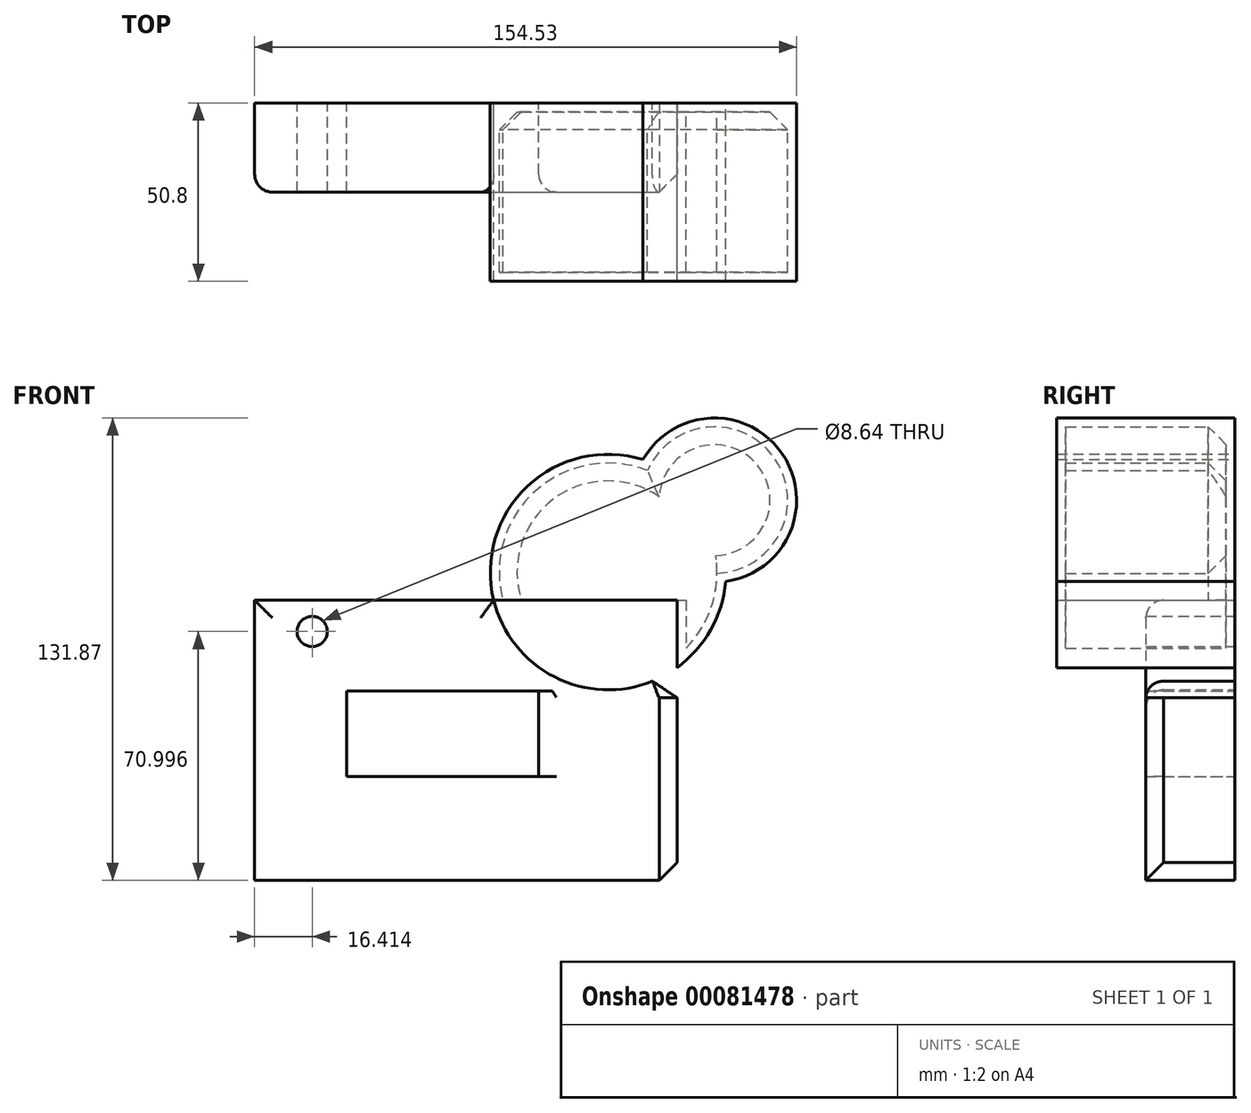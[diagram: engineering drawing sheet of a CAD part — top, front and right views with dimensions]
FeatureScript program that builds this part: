
annotation { "Feature Type Name" : "Feature", "Feature Type Description" : "" }
export const myFeature = defineFeature(function(context is Context, id is Id, definition is map)
    precondition{}
    {
        {
            var Q0;
            Q0=qCreatedBy(makeId("Front.planeOp"),FACE);
            var sketch = newSketch(context, id + "F0", { "sketchPlane" : qUnion([Q0])});
            skLineSegment(sketch, "E0.bottom", {"start": v(-57.98, 39.34) * mm, "end": v(62.44, 39.34) * mm});
            skLineSegment(sketch, "E0.top", {"start": v(-57.98, -40.58) * mm, "end": v(62.44, -40.58) * mm});
            skLineSegment(sketch, "E0.left", {"start": v(-57.98, 39.34) * mm, "end": v(-57.98, -40.58) * mm});
            skLineSegment(sketch, "E0.right", {"start": v(62.44, 39.34) * mm, "end": v(62.44, -40.58) * mm});
            skCircle(sketch, "E1", {"center": v(73.14, 67.88) * mm, "radius": 23.41 * mm});
            skCircle(sketch, "E2", {"center": v(42.81, 47.36) * mm, "radius": 33.59 * mm});
            skCircle(sketch, "E3", {"center": v(-41.57, 30.42) * mm, "radius": 4.32 * mm});
            skLineSegment(sketch, "E4.bottom", {"start": v(-31.75, 13.47) * mm, "end": v(23.01, 13.47) * mm});
            skLineSegment(sketch, "E4.top", {"start": v(-31.75, -10.97) * mm, "end": v(23.01, -10.97) * mm});
            skLineSegment(sketch, "E4.left", {"start": v(-31.75, 13.47) * mm, "end": v(-31.75, -10.97) * mm});
            skLineSegment(sketch, "E4.right", {"start": v(23.01, 13.47) * mm, "end": v(23.01, -10.97) * mm});
            skLineSegment(sketch, "E5.bottom", {"start": v(-31.75, -10.97) * mm, "end": v(-31.75, -10.97) * mm});
            skLineSegment(sketch, "E5.top", {"start": v(-31.75, -9.19) * mm, "end": v(-31.75, -9.19) * mm});
            skLineSegment(sketch, "E5.left", {"start": v(-31.75, -10.97) * mm, "end": v(-31.75, -9.19) * mm});
            skLineSegment(sketch, "E5.right", {"start": v(-31.75, -10.97) * mm, "end": v(-31.75, -9.19) * mm});
            skSolve(sketch);
        }
        {
            var Q0;
            {var subQ6=sQuery(id+"F0.wireOp",EDGE,"E0.top");Q0=makeQuery(id+"F0.imprint","IMPRINT",FACE,{"disambiguationData":[TD([[makeQuery(id+"F0.imprint","IMPRINT",EDGE,{"derivedFrom":subQ6}),1.0]])]});}
            var Q1;
            {var subQ0=sQuery(id+"F0.wireOp",EDGE,"E2");var subQ1=sQuery(id+"F0.wireOp",EDGE,"E1");var subQ2=makeQuery(id+"F0.imprint","INTERSECT",VERTEX,{"disambiguationData":[OD(0.0)],"derivedFrom":[subQ1,subQ0]});Q1=makeQuery(id+"F0.imprint","IMPRINT",FACE,{"disambiguationData":[TD([[makeQuery(id+"F0.imprint","IMPRINT",EDGE,{"disambiguationData":[TD([[subQ2,-1.0]])],"derivedFrom":subQ1}),1.0]])]});}
            var Q2;
            {var subQ0=sQuery(id+"F0.wireOp",EDGE,"E2");var subQ1=sQuery(id+"F0.wireOp",EDGE,"E1");var subQ2=makeQuery(id+"F0.imprint","INTERSECT",VERTEX,{"disambiguationData":[OD(0.0)],"derivedFrom":[subQ1,subQ0]});Q2=makeQuery(id+"F0.imprint","IMPRINT",FACE,{"disambiguationData":[TD([[makeQuery(id+"F0.imprint","IMPRINT",EDGE,{"disambiguationData":[TD([[subQ2,1.0]])],"derivedFrom":subQ1}),1.0]])]});}
            var Q3;
            {var subQ1=sQuery(id+"F0.wireOp",EDGE,"E0.bottom");var subQ5=sQuery(id+"F0.wireOp",EDGE,"E0.right");var subQ6=makeQuery(id+"F0.imprint","INTERSECT",VERTEX,{"derivedFrom":[subQ1,subQ5]});Q3=makeQuery(id+"F0.imprint","IMPRINT",FACE,{"disambiguationData":[TD([[makeQuery(id+"F0.imprint","IMPRINT",EDGE,{"disambiguationData":[TD([[subQ6,1.0]])],"derivedFrom":subQ1}),1.0]])]});}
            extrude(context, id + "F1", {"entities" : qUnion([Q0, Q1, Q2, Q3]), "depth" : 25.4 * mm});
        }
        {
            var Q0;
            Q0=makeQuery(id+"F1.opExtrude","CAP_FACE",FACE,{"disambiguationData":[OSD([sQuery(id+"F0.wireOp",EDGE,"E0.bottom"),sQuery(id+"F0.wireOp",EDGE,"E0.right"),sQuery(id+"F0.wireOp",EDGE,"E1"),sQuery(id+"F0.wireOp",EDGE,"E2")])],"isStart":false});
            extrude(context, id + "F2", {"entities" : qUnion([Q0]), "operationType" : NewBodyOperationType.ADD, "depth" : 25.4 * mm});
        }
        {
            var Q0;
            {var subQ0=sQuery(id+"F0.wireOp",EDGE,"E0.bottom");Q0=makeQuery(id+"F1.opExtrude","CAP_EDGE",EDGE,{"disambiguationData":[OSD([subQ0]),TDD([makeQuery(id+"F0.imprint","IMPRINT",EDGE,{"disambiguationData":[TD([[makeQuery(id+"F0.imprint","INTERSECT",VERTEX,{"derivedFrom":[subQ0,sQuery(id+"F0.wireOp",EDGE,"E0.left")]}),-1.0]])],"derivedFrom":subQ0})])],"isStart":false});}
            var Q1;
            Q1=makeQuery(id+"F1.opExtrude","CAP_EDGE",EDGE,{"disambiguationData":[OSD([sQuery(id+"F0.wireOp",EDGE,"E0.left")])],"isStart":false});
            var Q2;
            Q2=makeQuery(id+"F1.opExtrude","CAP_EDGE",EDGE,{"disambiguationData":[OSD([sQuery(id+"F0.wireOp",EDGE,"E4.right")])],"isStart":false});
            var Q3;
            {var subQ0=sQuery(id+"F0.wireOp",EDGE,"E2");Q3=makeQuery(id+"F1.opExtrude","CAP_EDGE",EDGE,{"disambiguationData":[OSD([subQ0]),TDD([makeQuery(id+"F0.imprint","IMPRINT",EDGE,{"disambiguationData":[TD([[makeQuery(id+"F0.imprint","INTERSECT",VERTEX,{"derivedFrom":[sQuery(id+"F0.wireOp",EDGE,"E0.bottom"),subQ0]}),-1.0]])],"derivedFrom":subQ0})])],"isStart":false});}
            fillet(context, id + "F3", {"entities" : qUnion([Q0, Q1, Q2, Q3]), "radius" : 5.08 * mm, "tangentPropagation" : true, "allowEdgeOverflow" : false});
        }
        {
            var Q0;
            {var subQ0=sQuery(id+"F0.wireOp",EDGE,"E0.bottom");Q0=makeQuery(id+"F2.boolean.opBoolean","MERGE",FACE,{"derivedFrom":[makeQuery(id+"F1.opExtrude","SWEPT_FACE",FACE,{"disambiguationData":[OSD([subQ0]),TDD([makeQuery(id+"F0.imprint","IMPRINT",EDGE,{"disambiguationData":[TD([[makeQuery(id+"F0.imprint","INTERSECT",VERTEX,{"derivedFrom":[subQ0,sQuery(id+"F0.wireOp",EDGE,"E0.right")]}),1.0]])],"derivedFrom":subQ0})])]}),makeQuery(id+"F2.opExtrude","SWEPT_FACE",FACE,{"disambiguationData":[OSD([subQ0])]})]});}
            shell(context, id + "F4", {"entities" : qUnion([Q0]), "thickness" : 2.54 * mm});
        }
        {
            var Q0;
            {var subQ0=sQuery(id+"F0.wireOp",EDGE,"E2");Q0=makeQuery(id+"F4.opShell","OFFSET_EDGE",EDGE,{"disambiguationData":[OSD([subQ0]),TDD([makeQuery(id+"F1.opExtrude","CAP_EDGE",EDGE,{"disambiguationData":[OSD([subQ0]),TDD([makeQuery(id+"F0.imprint","IMPRINT",EDGE,{"disambiguationData":[TD([[makeQuery(id+"F0.imprint","INTERSECT",VERTEX,{"derivedFrom":[sQuery(id+"F0.wireOp",EDGE,"E0.bottom"),subQ0]}),1.0]])],"derivedFrom":subQ0})])],"isStart":true})])]});}
            var Q1;
            {var subQ0=sQuery(id+"F0.wireOp",EDGE,"E1");Q1=makeQuery(id+"F4.opShell","OFFSET_EDGE",EDGE,{"disambiguationData":[OSD([subQ0]),TDD([makeQuery(id+"F1.opExtrude","CAP_EDGE",EDGE,{"disambiguationData":[OSD([subQ0])],"isStart":true})])]});}
            chamfer(context, id + "F5", {"entities" : qUnion([Q0, Q1]), "width" : 5.08 * mm, "tangentPropagation" : true});
        }
        {
            var Q0;
            {var subQ0=sQuery(id+"F0.wireOp",EDGE,"E0.right");Q0=makeQuery(id+"F1.opExtrude","CAP_EDGE",EDGE,{"disambiguationData":[OSD([subQ0]),TDD([makeQuery(id+"F0.imprint","IMPRINT",EDGE,{"disambiguationData":[TD([[makeQuery(id+"F0.imprint","INTERSECT",VERTEX,{"derivedFrom":[sQuery(id+"F0.wireOp",EDGE,"E0.top"),subQ0]}),1.0]])],"derivedFrom":subQ0})])],"isStart":false});}
            var Q1;
            Q1=makeQuery(id+"F1.opExtrude","SWEPT_EDGE",EDGE,{"disambiguationData":[OSD([sQuery(id+"F0.wireOp",EDGE,"E0.top"),sQuery(id+"F0.wireOp",EDGE,"E0.right")])]});
            chamfer(context, id + "F6", {"entities" : qUnion([Q0, Q1]), "width" : 5.08 * mm, "tangentPropagation" : true});
        }
    });
